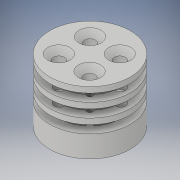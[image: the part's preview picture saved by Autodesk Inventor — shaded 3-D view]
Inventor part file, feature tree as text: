
AUTODESK INVENTOR PART (.ipt)
format: ipt  version: 2019 (Build 230136000, 136)  size: 297,472 bytes
history: native  units: mm
features: sketch x8, extrude x6, other x3, revolve x1, hole x1
ambient origin geometry x8: Origin, YZ Plane, XZ Plane, XY Plane, X Axis, Y Axis, Z Axis, Center Point
bodies: Body1 (feature_tree)
feature tree (19):
  other  "Bryła1"
  extrude  "Wyciągnięcie proste1"  Depth=20.0mm
  other  "Płaszczyzna konstrukcyjna1"
  revolve  "Obrót1"
  extrude  "Wyciągnięcie proste6"  Depth=25.0mm
  extrude  "Wyciągnięcie proste7"  Depth=5.0mm TaperAngle=0.0deg
  extrude  "Wyciągnięcie proste8"  Depth=2.5mm
  other  "Płaszczyzna konstrukcyjna2"
  extrude  "Wyciągnięcie proste9"  Depth=19.5mm
  extrude  "Wyciągnięcie proste10"  Depth=3.0mm
  hole  "Otwór1"  [1 undecoded]
  sketch  "Szkic1"
  sketch  "Szkic5"
  sketch  "Szkic7"
  sketch  "Szkic8"
  sketch  "Szkic9"
  sketch  "Szkic10"
  sketch  "Szkic11"
  sketch  "Szkic12"
note: 1 required parameter value undecoded (feature->parameter linkage not recoverable at this tier; creation-order binding heuristic only, values carry confidence <= 0.55)
